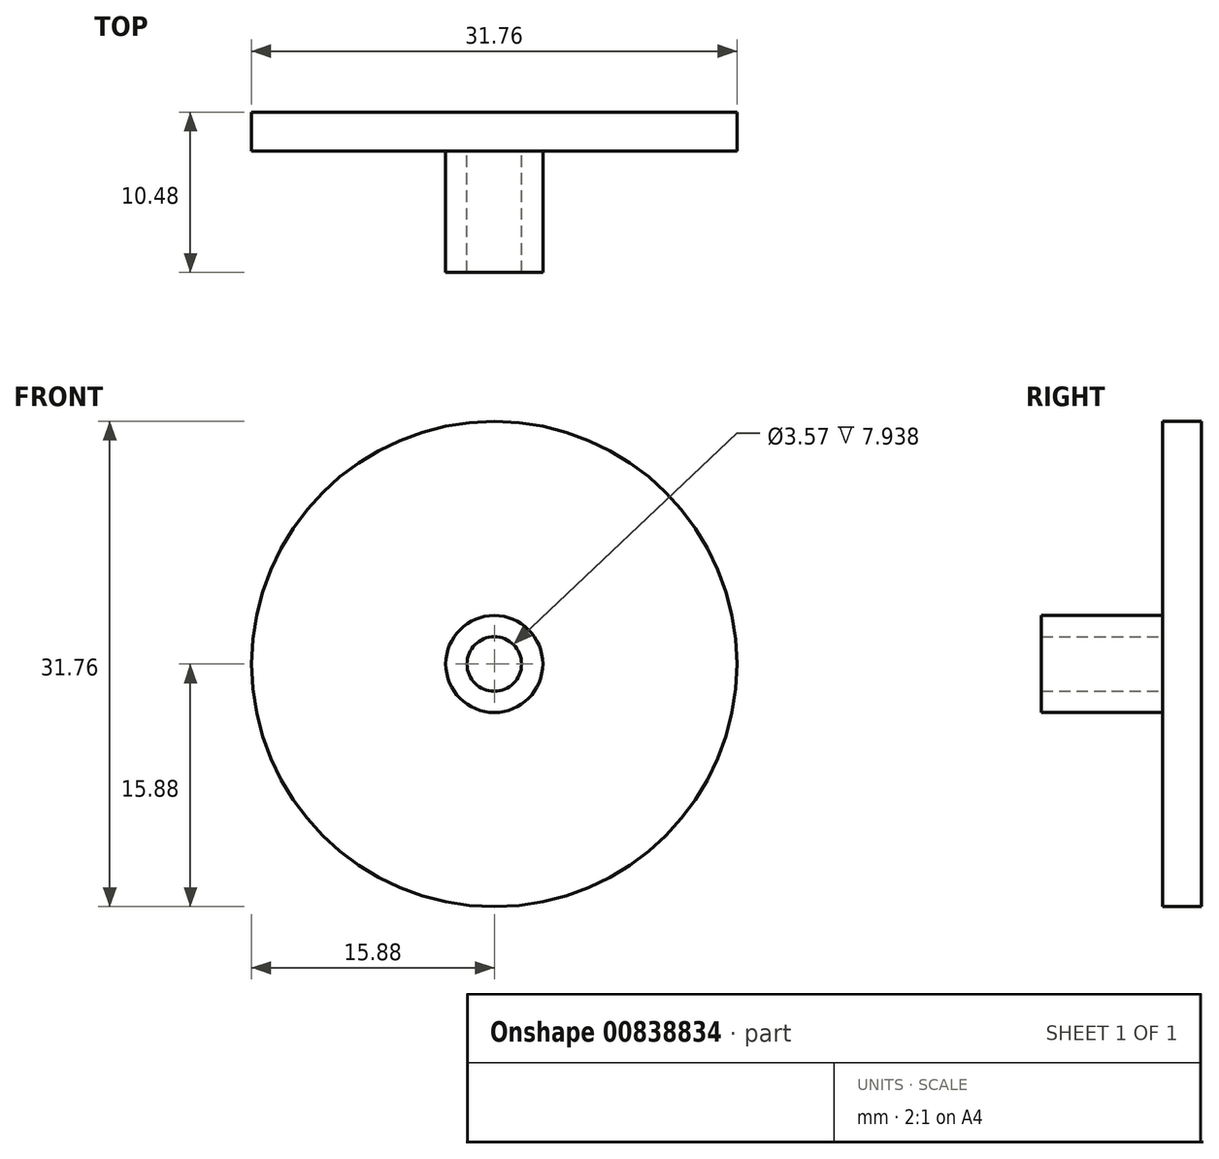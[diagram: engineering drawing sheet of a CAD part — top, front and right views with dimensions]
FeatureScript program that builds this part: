
annotation { "Feature Type Name" : "Feature", "Feature Type Description" : "" }
export const myFeature = defineFeature(function(context is Context, id is Id, definition is map)
    precondition{}
    {
        {
            var Q0;
            Q0=qCreatedBy(makeId("Front.planeOp"),FACE);
            var sketch = newSketch(context, id + "F0", { "sketchPlane" : qUnion([Q0])});
            skCircle(sketch, "E0", {"center": v(0, 0) * mm, "radius": 15.88 * mm});
            skSolve(sketch);
        }
        {
            var Q0;
            Q0 = qSketchRegion(id + "F0", true);
            extrude(context, id + "F1", {"entities" : qUnion([Q0]), "depth" : 2.54 * mm, "offsetDistance" : 25.4 * mm});
        }
        {
            var Q0;
            Q0=makeQuery(id+"F1.opExtrude","CAP_FACE",FACE,{"disambiguationData":[OSD([sQuery(id+"F0.wireOp",EDGE,"E0")])],"isStart":false});
            var sketch = newSketch(context, id + "F2", { "sketchPlane" : qUnion([Q0])});
            skCircle(sketch, "E1", {"center": v(0, 0) * mm, "radius": 3.18 * mm});
            skCircle(sketch, "E2", {"center": v(0, 0) * mm, "radius": 1.79 * mm});
            skSolve(sketch);
        }
        {
            var Q0;
            Q0=makeQuery(id+"F2.imprint","IMPRINT",FACE,{"disambiguationData":[TD([[makeQuery(id+"F2.imprint","IMPRINT",EDGE,{"derivedFrom":sQuery(id+"F2.wireOp",EDGE,"E1")}),1.0]])]});
            extrude(context, id + "F3", {"entities" : qUnion([Q0]), "operationType" : NewBodyOperationType.ADD, "depth" : 7.94 * mm, "offsetDistance" : 25.4 * mm});
        }
    });
